FCSTD DOCUMENT  (FreeCAD 1.0R39319 (Git))
Label: Case-hole-cutouts
License: All rights reserved
LicenseURL: https://en.wikipedia.org/wiki/All_rights_reserved
objects: Sketcher::SketchObject×1
note: 2 computed .brp shape members not serialized (recipe doc carries the construction recipe); baked Part::Feature solids carry a one-line shape summary decoded from their .brp

FEATURE [Sketcher::SketchObject] Sketch
  ArcFitTolerance = 1e-06
  FullyConstrained = true
  MakeInternals = false
  sketch-geometry (9):
    g0: Circle [constr] CenterX=-19 CenterY=-19 CenterZ=0 NormalX=0 NormalY=0 NormalZ=1 AngleXU=0 Radius=6.8
    g1: Circle [constr] CenterX=19 CenterY=-19 CenterZ=0 NormalX=0 NormalY=0 NormalZ=1 AngleXU=0 Radius=6.8
    g2: Circle CenterX=0 CenterY=-37 CenterZ=0 NormalX=0 NormalY=0 NormalZ=1 AngleXU=0 Radius=6
    g3: ArcOfCircle CenterX=-19 CenterY=-19 CenterZ=0 NormalX=0 NormalY=0 NormalZ=1 AngleXU=0 Radius=6.8 StartAngle=3.56483 EndAngle=9.00154
    g4: LineSegment StartX=-25.2 StartY=-16.2072 StartZ=0 EndX=-25.2 EndY=-21.7928 EndZ=0
    g5: LineSegment [constr] StartX=-19 StartY=-19 StartZ=0 EndX=-12.2 EndY=-19 EndZ=0
    g6: LineSegment [constr] StartX=19 StartY=-19 StartZ=0 EndX=25.8 EndY=-19 EndZ=0
    g7: ArcOfCircle CenterX=19 CenterY=-19 CenterZ=0 NormalX=0 NormalY=0 NormalZ=1 AngleXU=0 Radius=6.8 StartAngle=3.56483 EndAngle=9.00154
    g8: LineSegment StartX=12.8 StartY=-21.7928 StartZ=0 EndX=12.8 EndY=-16.2072 EndZ=0
  constraints (26):
    c: PointOnObject(g2,g-2)
    c: Diameter(g2) = 12
    c: DistanceY(g2,g-1) = 37
    c: Symmetric(g0,g1,g-2)
    c: DistanceX(g0,g-1) = 19
    c: Equal(g1,g0)
    c: Diameter(g0) = 13.6
    c: Coincident(g3,g0)
    c: PointOnObject(g3,g0)
    c: Coincident(g4,g3)
    c: Coincident(g4,g3)
    c: Vertical(g4)
    c: Coincident(g5,g0)
    c: PointOnObject(g5,g3)
    c: Horizontal(g5)
    c: DistanceX(g3,g5) = 13
    c: DistanceY(g0,g-1) = 19
    c: Coincident(g6,g1)
    c: PointOnObject(g6,g1)
    c: Horizontal(g6)
    c: Coincident(g7,g1)
    c: PointOnObject(g7,g1)
    c: Coincident(g8,g7)
    c: Coincident(g8,g7)
    c: Vertical(g8)
    c: DistanceX(g7,g6) = 13
